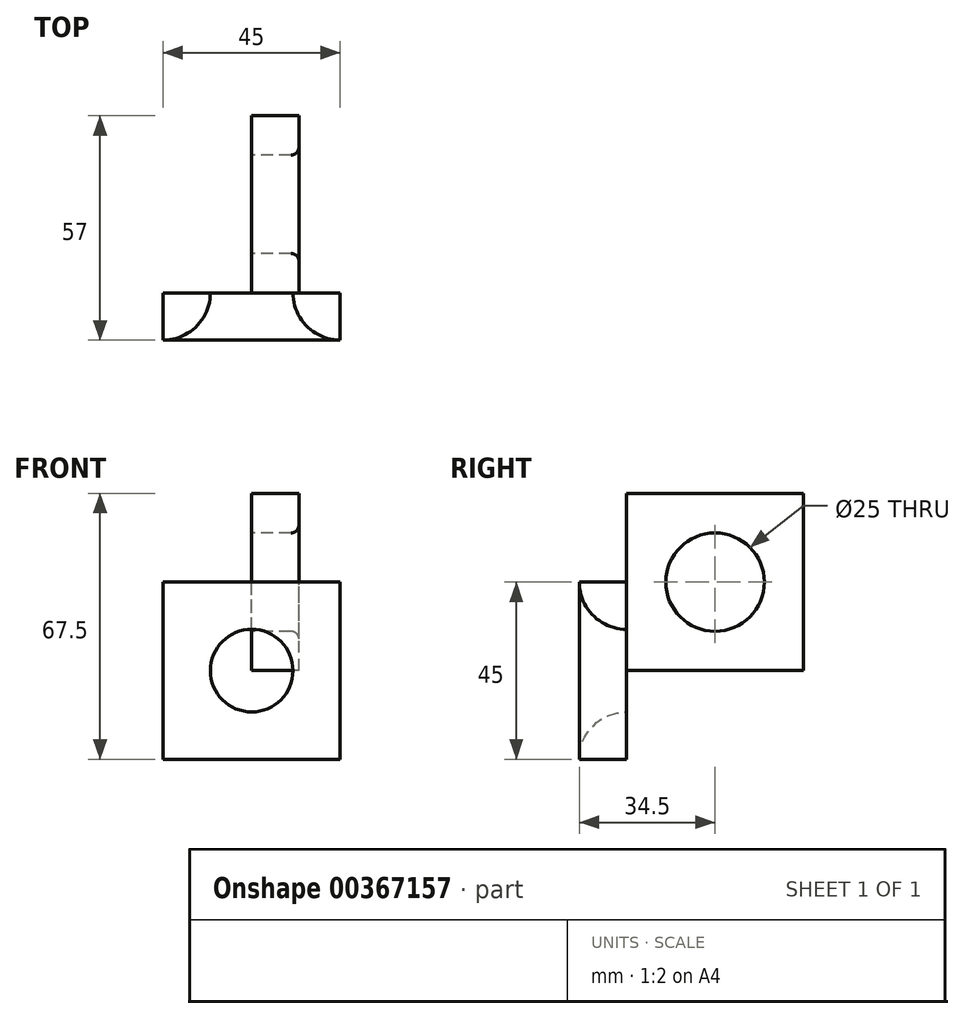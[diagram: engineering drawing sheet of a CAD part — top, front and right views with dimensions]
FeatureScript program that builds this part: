
annotation { "Feature Type Name" : "Feature", "Feature Type Description" : "" }
export const myFeature = defineFeature(function(context is Context, id is Id, definition is map)
    precondition{}
    {
        {
            var Q0;
            Q0=qCreatedBy(makeId("Front.planeOp"),FACE);
            var sketch = newSketch(context, id + "F0", { "sketchPlane" : qUnion([Q0])});
            skCircle(sketch, "E0", {"center": v(0, 0) * mm, "radius": 10.5 * mm});
            skLineSegment(sketch, "E1.bottom", {"start": v(22.5, 22.5) * mm, "end": v(-22.5, 22.5) * mm});
            skLineSegment(sketch, "E1.top", {"start": v(22.5, -22.5) * mm, "end": v(-22.5, -22.5) * mm});
            skLineSegment(sketch, "E1.left", {"start": v(22.5, 22.5) * mm, "end": v(22.5, -22.5) * mm});
            skLineSegment(sketch, "E1.right", {"start": v(-22.5, 22.5) * mm, "end": v(-22.5, -22.5) * mm});
            skSolve(sketch);
        }
        {
            var Q0;
            Q0=makeQuery(id+"F0.imprint","IMPRINT",FACE,{"disambiguationData":[TD([[makeQuery(id+"F0.imprint","IMPRINT",EDGE,{"derivedFrom":sQuery(id+"F0.wireOp",EDGE,"E0")}),-1.0]])]});
            extrude(context, id + "F1", {"entities" : qUnion([Q0]), "depth" : 12 * mm});
        }
        {
            var Q0;
            Q0=makeQuery(id+"F1.opExtrude","CAP_EDGE",EDGE,{"disambiguationData":[OSD([sQuery(id+"F0.wireOp",EDGE,"E0")])],"isStart":false});
            fillet(context, id + "F2", {"entities" : qUnion([Q0]), "radius" : 12 * mm, "tangentPropagation" : true, "allowEdgeOverflow" : false});
        }
        {
            var Q0;
            Q0=qCreatedBy(makeId("Right.planeOp"),FACE);
            var sketch = newSketch(context, id + "F3", { "sketchPlane" : qUnion([Q0])});
            skLineSegment(sketch, "E2.bottom", {"start": v(0, 0) * mm, "end": v(45, 0) * mm});
            skLineSegment(sketch, "E2.top", {"start": v(0, 45) * mm, "end": v(45, 45) * mm});
            skLineSegment(sketch, "E2.left", {"start": v(0, 0) * mm, "end": v(0, 45) * mm});
            skLineSegment(sketch, "E2.right", {"start": v(45, 0) * mm, "end": v(45, 45) * mm});
            skCircle(sketch, "E3", {"center": v(22.5, 22.5) * mm, "radius": 12.5 * mm});
            skPoint(sketch, "E3.centerSnap0", {"position": v(45, 22.5) * mm});
            skPoint(sketch, "E3.centerSnap1", {"position": v(22.5, 45) * mm});
            skSolve(sketch);
        }
        {
            var Q0;
            Q0=makeQuery(id+"F3.imprint","IMPRINT",FACE,{"disambiguationData":[TD([[makeQuery(id+"F3.imprint","IMPRINT",EDGE,{"derivedFrom":sQuery(id+"F3.wireOp",EDGE,"E2.bottom")}),1.0]])]});
            extrude(context, id + "F4", {"entities" : qUnion([Q0]), "depth" : 12 * mm});
        }
        {
            var Q0;
            Q0=makeQuery(id+"F4.opExtrude","CAP_EDGE",EDGE,{"disambiguationData":[OSD([sQuery(id+"F3.wireOp",EDGE,"E3")])],"isStart":false});
            fillet(context, id + "F5", {"entities" : qUnion([Q0]), "radius" : 2 * mm, "tangentPropagation" : true, "allowEdgeOverflow" : false});
        }
    });
